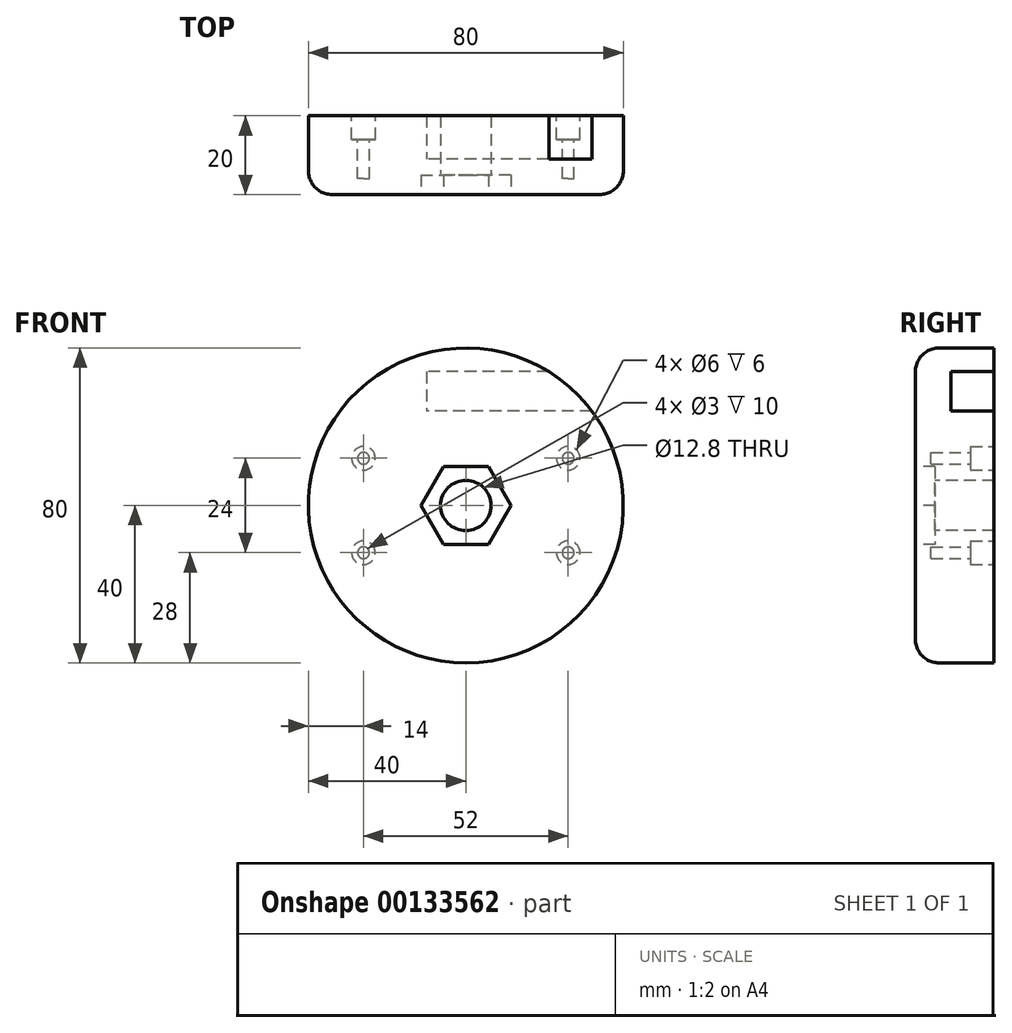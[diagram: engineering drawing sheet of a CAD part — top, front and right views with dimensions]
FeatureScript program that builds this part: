
annotation { "Feature Type Name" : "Feature", "Feature Type Description" : "" }
export const myFeature = defineFeature(function(context is Context, id is Id, definition is map)
    precondition{}
    {
        {
            var Q0;
            Q0=qCreatedBy(makeId("Front.planeOp"),FACE);
            var sketch = newSketch(context, id + "F0", { "sketchPlane" : qUnion([Q0])});
            skCircle(sketch, "E0", {"center": v(0, 0) * mm, "radius": 40 * mm});
            skSolve(sketch);
        }
        {
            var Q0;
            Q0=qSketchRegion(id+"F0",true);
            extrude(context, id + "F1", {"entities" : qUnion([Q0]), "depth" : 20 * mm});
        }
        {
            var Q0;
            Q0=qCreatedBy(makeId("Right.planeOp"),FACE);
            var sketch = newSketch(context, id + "F2", { "sketchPlane" : qUnion([Q0])});
            skLineSegment(sketch, "E1.bottom", {"start": v(0, 34) * mm, "end": v(-11, 34) * mm});
            skLineSegment(sketch, "E1.top", {"start": v(0, 24) * mm, "end": v(-11, 24) * mm});
            skLineSegment(sketch, "E1.left", {"start": v(0, 34) * mm, "end": v(0, 24) * mm});
            skLineSegment(sketch, "E1.right", {"start": v(-11, 34) * mm, "end": v(-11, 24) * mm});
            skSolve(sketch);
        }
        {
            var Q0;
            Q0=qSketchRegion(id+"F2",true);
            extrude(context, id + "F3", {"entities" : qUnion([Q0]), "operationType" : NewBodyOperationType.REMOVE, "depth" : 50 * mm, "hasSecondDirection" : true, "secondDirectionOppositeDirection" : true, "secondDirectionDepth" : 10 * mm});
        }
        {
            var Q0;
            Q0=makeQuery(id+"F1.opExtrude","CAP_EDGE",EDGE,{"disambiguationData":[OSD([sQuery(id+"F0.wireOp",EDGE,"E0")])],"isStart":false});
            fillet(context, id + "F4", {"entities" : qUnion([Q0]), "radius" : 6 * mm, "tangentPropagation" : true, "allowEdgeOverflow" : false});
        }
        {
            var Q0;
            Q0=makeQuery(id+"F1.opExtrude","CAP_FACE",FACE,{"disambiguationData":[OSD([sQuery(id+"F0.wireOp",EDGE,"E0")])],"isStart":false});
            var sketch = newSketch(context, id + "F5", { "sketchPlane" : qUnion([Q0])});
            skCircle(sketch, "E2.cCircle", {"center": v(0, 0) * mm, "radius": 9.9 * mm, "construction": true});
            skLineSegment(sketch, "E2.0", {"start": v(5.72, -9.9) * mm, "end": v(-5.72, -9.9) * mm});
            skLineSegment(sketch, "E2.1", {"start": v(-5.72, -9.9) * mm, "end": v(-11.43, 0) * mm});
            skLineSegment(sketch, "E2.2", {"start": v(-11.43, 0) * mm, "end": v(-5.72, 9.9) * mm});
            skLineSegment(sketch, "E2.3", {"start": v(-5.72, 9.9) * mm, "end": v(5.72, 9.9) * mm});
            skLineSegment(sketch, "E2.4", {"start": v(5.72, 9.9) * mm, "end": v(11.43, 0) * mm});
            skLineSegment(sketch, "E2.5", {"start": v(11.43, 0) * mm, "end": v(5.72, -9.9) * mm});
            skPoint(sketch, "E2.0.midPoint", {"position": v(0, -9.9) * mm});
            skSolve(sketch);
        }
        {
            var Q0;
            Q0=qSketchRegion(id+"F5",true);
            extrude(context, id + "F6", {"entities" : qUnion([Q0]), "operationType" : NewBodyOperationType.REMOVE, "oppositeDirection" : true, "depth" : 5 * mm});
        }
        {
            var Q0;
            Q0=makeQuery(id+"F6.boolean.opBoolean","COPY",FACE,{"derivedFrom":makeQuery(id+"F6.opExtrude","CAP_FACE",FACE,{"disambiguationData":[OSD([sQuery(id+"F5.wireOp",EDGE,"E2.0"),sQuery(id+"F5.wireOp",EDGE,"E2.1"),sQuery(id+"F5.wireOp",EDGE,"E2.2"),sQuery(id+"F5.wireOp",EDGE,"E2.3"),sQuery(id+"F5.wireOp",EDGE,"E2.4"),sQuery(id+"F5.wireOp",EDGE,"E2.5")])],"isStart":false})});
            var sketch = newSketch(context, id + "F7", { "sketchPlane" : qUnion([Q0])});
            skCircle(sketch, "E3", {"center": v(0, 0) * mm, "radius": 6.4 * mm});
            skSolve(sketch);
        }
        {
            var Q0;
            Q0=qSketchRegion(id+"F7",true);
            extrude(context, id + "F8", {"entities" : qUnion([Q0]), "operationType" : NewBodyOperationType.REMOVE, "oppositeDirection" : true, "depth" : 25 * mm});
        }
        {
            var Q0;
            Q0=qCreatedBy(makeId("Front.planeOp"),FACE);
            var sketch = newSketch(context, id + "F9", { "sketchPlane" : qUnion([Q0])});
            skCircle(sketch, "E4", {"center": v(26, 12) * mm, "radius": 1.5 * mm});
            skCircle(sketch, "E5.MirrorC", {"center": v(-26, 12) * mm, "radius": 1.5 * mm});
            skCircle(sketch, "E6.MirrorC", {"center": v(-26, -12) * mm, "radius": 1.5 * mm});
            skCircle(sketch, "E7.MirrorC", {"center": v(26, -12) * mm, "radius": 1.5 * mm});
            skSolve(sketch);
        }
        {
            var Q0;
            Q0 = qSketchRegion(id + "F9", true);
            extrude(context, id + "F10", {"entities" : qUnion([Q0]), "operationType" : NewBodyOperationType.REMOVE, "depth" : 16 * mm});
        }
        {
            var Q0;
            Q0=makeQuery(id+"F1.opExtrude","CAP_FACE",FACE,{"disambiguationData":[OSD([sQuery(id+"F0.wireOp",EDGE,"E0")])],"isStart":true});
            var sketch = newSketch(context, id + "F11", { "sketchPlane" : qUnion([Q0])});
            skCircle(sketch, "E8", {"center": v(-26, 12) * mm, "radius": 3 * mm});
            skCircle(sketch, "E9.MirrorC", {"center": v(26, 12) * mm, "radius": 3 * mm});
            skCircle(sketch, "E10.MirrorC", {"center": v(26, -12) * mm, "radius": 3 * mm});
            skCircle(sketch, "E11.MirrorC", {"center": v(-26, -12) * mm, "radius": 3 * mm});
            skSolve(sketch);
        }
        {
            var Q0;
            Q0 = qSketchRegion(id + "F11", true);
            extrude(context, id + "F12", {"entities" : qUnion([Q0]), "operationType" : NewBodyOperationType.REMOVE, "oppositeDirection" : true, "depth" : 6 * mm});
        }
    });
